# Revit family: Schlüter-KERDI-LINE-D E Fliesenträger D
name_source: partatom
category: Sanitärinstallationen
revit_build: Autodesk Revit 2018 (Build: 20170223_1515(x64)
units: mm (PartAtom-declared; Revit-internal decimal feet)

## family parameters
Arbeitsebenenbasiert = Nein
Beim Laden mit Abzugskörper schneiden = Nein
Bemaßung runder Anschluss = Durchmesser verwenden
Gemeinsam genutzt = Nein
Immer vertikal = Ja
OmniClass-Nummer = 23.45.00.00
OmniClass-Titel = Sanitary, Laundry, and Cleaning Equipment
Raumberechnungspunkt = Nein
Teiletyp = Normal

## types (15) — shared parameters
Abwasserrohrverbindung = Nein
HW-Verbindung = Nein
Height = 12 mm  [stored 0.0393701 ft]
KW-Verbindung = Nein
Lüftungsverbindung = Nein
zero-valued in all types: CWFU, HWFU, Kosten, Länge [mm] Number, WFU

## per-type parameters (varying)
| type | Ausführung Abdeckung | Ausführung Text | BIM | BIMSITE_PRODUCT_ID | Beschreibung | Breite [mm] Number | Datenblatt | Datenblatt 1 | Datenblatt 2 | Datenblatt 3 | Handbuch | HeinzeBIM | Hersteller | Ist System | Ist Zubehör | Length | Länge [mm] | Mit Rahmen | Produktseite | Typname | URL | Werkstoff Text | Werkstoff-Nr |
| KLD E 50 |  |  |  |  |  | 0 |  |  |  |  |  |  |  | Ja | Ja | 490 mm  [stored 1.60761 ft] |  | Ja |  |  |  |  |  |
| KLD E 60 |  |  |  |  |  | 0 |  |  |  |  |  |  |  | Ja | Ja | 590 mm |  | Ja |  |  |  |  |  |
| KLD E 70 |  |  |  |  |  | 0 |  |  |  |  |  |  |  | Ja | Ja | 690 mm |  | Ja |  |  |  |  |  |
| KLD E 80 |  |  |  |  |  | 0 |  |  |  |  |  |  |  | Ja | Ja | 790 mm |  | Ja |  |  |  |  |  |
| KLD E 90 |  |  |  |  |  | 0 |  |  |  |  |  |  |  | Ja | Ja | 890 mm |  | Ja |  |  |  |  |  |
| KLD E 100 |  |  |  |  |  | 0 |  |  |  |  |  |  |  | Ja | Ja | 990 mm |  | Ja |  |  |  |  |  |
| KLD E 110 |  |  |  |  |  | 0 |  |  |  |  |  |  |  | Ja | Ja | 1090 mm |  | Ja |  |  |  |  |  |
| KLD E 120 |  |  |  |  |  | 0 |  |  |  |  |  |  |  | Ja | Ja | 1190 mm |  | Ja |  |  |  |  |  |
| KLD E 130 |  |  |  |  |  | 0 |  |  |  |  |  |  |  | Ja | Ja | 1290 mm |  | Ja |  |  |  |  |  |
| KLD E 140 |  |  |  |  |  | 0 |  |  |  |  |  |  |  | Ja | Ja | 1390 mm |  | Ja |  |  |  |  |  |
| KLD E 150 |  |  |  |  |  | 0 |  |  |  |  |  |  |  | Ja | Ja | 1490 mm |  | Ja |  |  |  |  |  |
| KLD E 160 |  |  |  |  |  | 0 |  |  |  |  |  |  |  | Ja | Ja | 1590 mm |  | Ja |  |  |  |  |  |
| KLD E 170 |  |  |  |  |  | 0 |  |  |  |  |  |  |  | Ja | Ja | 1690 mm |  | Ja |  |  |  |  |  |
| KLD E 180 |  |  |  |  |  | 0 |  |  |  |  |  |  |  | Ja | Ja | 1790 mm |  | Ja |  |  |  |  |  |
| Schlüter-KERDI-LINE-D E Fliesenträger D | Abdeckplatte für wählbare Oberfläche | Belagträger D, universell für alle Belagstärken geeignet | https://media.live.bim.site Rost D_E.rfa | e84c9f3a68d5b7cdf634ee3298ca9f1a2c2fb242 | Schlüter-KERDI-LINE-D ist eine rahmenlose Rinnenabdeckung, passend zu Schlüter- KERDI-LINE Rinnenkörpern. Der Belagträger ist mit einem Vlies zur Verankerung des Fliesenklebers ausgestattet und universell für alle Belagstärken geeignet. Die Schlüter®-KERDI-LINE Rinnenkörper bestehen aus solidem Edelstahl und sind in Ausführungen für die horizontale oder vertikale Entwässerung verfügbar. Sie sind in 8 Längen, passend zu den systemgehörigen Rost-/Rahmen-Kombination (Designabdeckung geschlossen/ gelocht/ Fliesenmulde) und Belagträgern erhältlich. Die Schlüter®-KERDI-LINE Rinnenkörper sind so konzipiert, dass sie variabel sowohl im Wandbereich als auch in der Fläche eingebaut werden können. Die mehrseitig umklebte Schlüter®-KERDI-LINE-Manschette ermöglicht eine sichere Abdichtung. | 50 | https://media.live.bim.site | https://media.live.bim.site | https://media.live.bim.site | https://media.live.bim.site | https://media.live.bim.site | https://www.heinze.de | Schlüter-Systems | Nein | Nein | 490 mm  [stored 1.60761 ft] | [490:1790] | Nein | https://media.live.bim.site | Schlüter-KERDI-LINE-D E Fliesenträger D | https://www.schlueter.de | Edelstahl/rostfreier Stahl (V4A) | 1.4404 |

note: [stored X ft] marks values corroborated as IEEE doubles in the binary element streams (Revit-internal decimal feet)

## geometry (parser evidence)
native form markers: Sweep x2
no freeform markers — native parametric forms only
